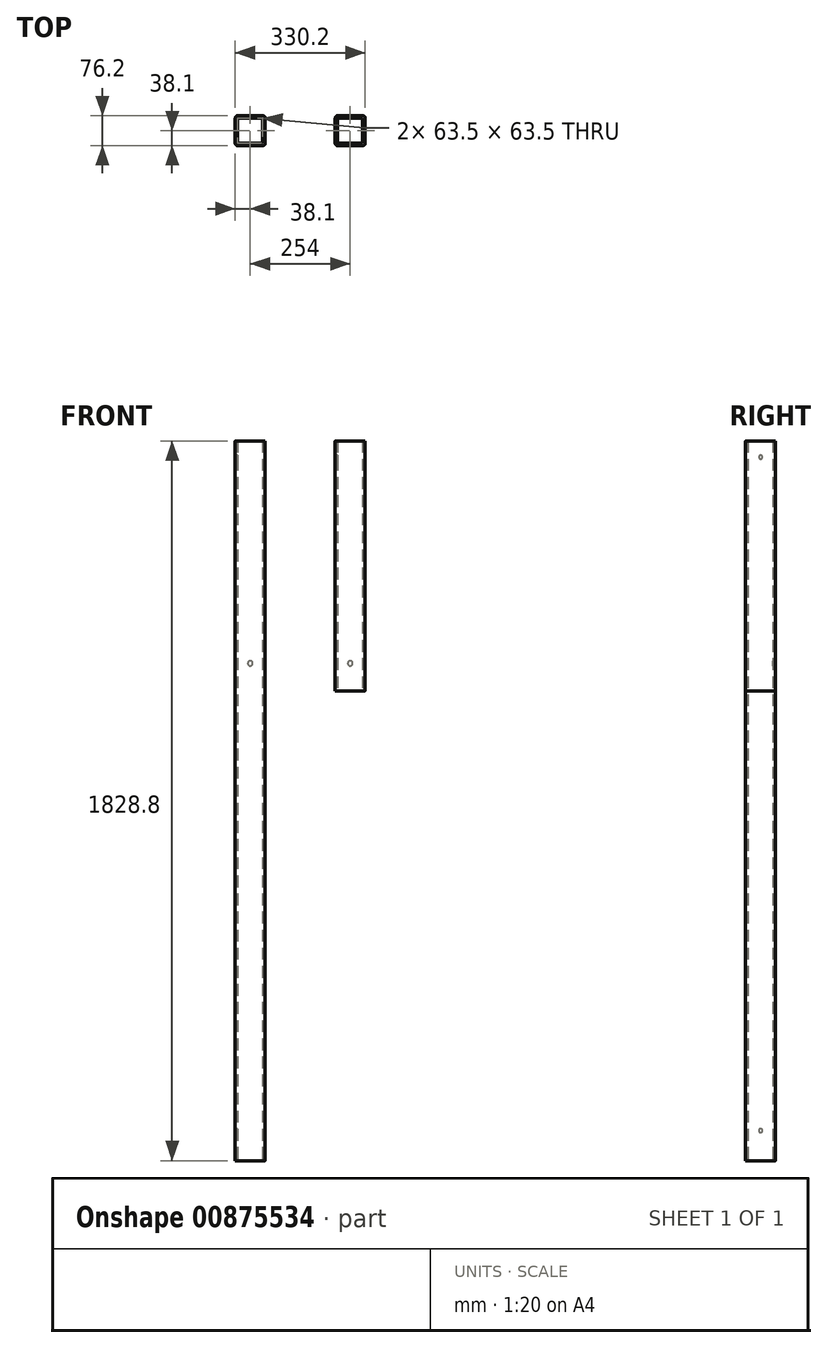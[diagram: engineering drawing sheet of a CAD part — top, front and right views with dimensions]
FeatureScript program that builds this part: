
annotation { "Feature Type Name" : "Feature", "Feature Type Description" : "" }
export const myFeature = defineFeature(function(context is Context, id is Id, definition is map)
    precondition{}
    {
        {
            var Q0;
            Q0=qCreatedBy(makeId("Top.planeOp"),FACE);
            var sketch = newSketch(context, id + "F0", { "sketchPlane" : qUnion([Q0])});
            skLineSegment(sketch, "E0.bottom", {"start": v(31.75, -38.1) * mm, "end": v(-31.75, -38.1) * mm});
            skLineSegment(sketch, "E0.top", {"start": v(31.75, 38.1) * mm, "end": v(-31.75, 38.1) * mm});
            skLineSegment(sketch, "E0.left", {"start": v(38.1, -31.75) * mm, "end": v(38.1, 31.75) * mm});
            skLineSegment(sketch, "E0.right", {"start": v(-38.1, -31.75) * mm, "end": v(-38.1, 31.75) * mm});
            skPoint(sketch, "E0.middle", {"position": v(0, 0) * mm});
            skLineSegment(sketch, "E1.bottom", {"start": v(31.75, -31.75) * mm, "end": v(-31.75, -31.75) * mm});
            skLineSegment(sketch, "E1.top", {"start": v(31.75, 31.75) * mm, "end": v(-31.75, 31.75) * mm});
            skLineSegment(sketch, "E1.left", {"start": v(31.75, -31.75) * mm, "end": v(31.75, 31.75) * mm});
            skLineSegment(sketch, "E1.right", {"start": v(-31.75, -31.75) * mm, "end": v(-31.75, 31.75) * mm});
            skPoint(sketch, "E2.visualSharp", {"position": v(-38.1, 38.1) * mm});
            skArc(sketch, "E2.filletArc", {"start": v(-31.75, 38.1) * mm, "mid": v(-36.24, 36.24) * mm, "end": v(-38.1, 31.75) * mm});
            skPoint(sketch, "E3.visualSharp", {"position": v(38.1, 38.1) * mm});
            skArc(sketch, "E3.filletArc", {"start": v(38.1, 31.75) * mm, "mid": v(36.24, 36.24) * mm, "end": v(31.75, 38.1) * mm});
            skPoint(sketch, "E4.visualSharp", {"position": v(38.1, -38.1) * mm});
            skArc(sketch, "E4.filletArc", {"start": v(31.75, -38.1) * mm, "mid": v(36.24, -36.24) * mm, "end": v(38.1, -31.75) * mm});
            skPoint(sketch, "E5.visualSharp", {"position": v(-38.1, -38.1) * mm});
            skArc(sketch, "E5.filletArc", {"start": v(-38.1, -31.75) * mm, "mid": v(-36.24, -36.24) * mm, "end": v(-31.75, -38.1) * mm});
            skSolve(sketch);
        }
        {
            var Q0;
            Q0=makeQuery(id+"F0.imprint","IMPRINT",FACE,{"disambiguationData":[TD([[makeQuery(id+"F0.imprint","IMPRINT",EDGE,{"derivedFrom":sQuery(id+"F0.wireOp",EDGE,"E0.bottom")}),-1.0]])]});
            extrude(context, id + "F1", {"entities" : qUnion([Q0]), "endBound" : BoundingType.SYMMETRIC, "depth" : 1828.8 * mm, "offsetDistance" : 25.4 * mm});
        }
        {
            var Q0;
            Q0=makeQuery(id+"F1.opExtrude","SWEPT_FACE",FACE,{"disambiguationData":[OSD([sQuery(id+"F0.wireOp",EDGE,"E0.top")])]});
            var sketch = newSketch(context, id + "F2", { "sketchPlane" : qUnion([Q0])});
            skCircle(sketch, "E6", {"center": v(0, 349.25) * mm, "radius": 6.35 * mm});
            skLineSegment(sketch, "E7", {"start": v(0, 914.4) * mm, "end": v(0, 349.25) * mm});
            skSolve(sketch);
        }
        {
            var Q0;
            Q0=makeQuery(id+"F2.imprint","IMPRINT",FACE,{"disambiguationData":[TD([[makeQuery(id+"F2.imprint","IMPRINT",EDGE,{"derivedFrom":sQuery(id+"F2.wireOp",EDGE,"E6")}),1.0]])]});
            var Q1;
            Q1=makeQuery(id+"F1.opExtrude","SWEPT_FACE",FACE,{"disambiguationData":[OSD([sQuery(id+"F0.wireOp",EDGE,"E1.top")])]});
            extrude(context, id + "F3", {"entities" : qUnion([Q0]), "operationType" : NewBodyOperationType.REMOVE, "endBound" : BoundingType.UP_TO_SURFACE, "oppositeDirection" : true, "depth" : 25.4 * mm, "endBoundEntityFace" : qUnion([Q1]), "offsetDistance" : 25.4 * mm});
        }
        {
            var Q0;
            Q0=makeQuery(id+"F1.opExtrude","SWEPT_FACE",FACE,{"disambiguationData":[OSD([sQuery(id+"F0.wireOp",EDGE,"E0.right")])]});
            var sketch = newSketch(context, id + "F4", { "sketchPlane" : qUnion([Q0])});
            skCircle(sketch, "E8", {"center": v(0, -838.2) * mm, "radius": 4.76 * mm});
            skLineSegment(sketch, "E9", {"start": v(0, -838.2) * mm, "end": v(0, -914.4) * mm});
            skSolve(sketch);
        }
        {
            var Q0;
            Q0=makeQuery(id+"F4.imprint","IMPRINT",FACE,{"disambiguationData":[TD([[makeQuery(id+"F4.imprint","IMPRINT",EDGE,{"derivedFrom":sQuery(id+"F4.wireOp",EDGE,"E8")}),1.0]])]});
            var Q1;
            Q1=makeQuery(id+"F1.opExtrude","SWEPT_FACE",FACE,{"disambiguationData":[OSD([sQuery(id+"F0.wireOp",EDGE,"E1.right")])]});
            extrude(context, id + "F5", {"entities" : qUnion([Q0]), "operationType" : NewBodyOperationType.REMOVE, "endBound" : BoundingType.UP_TO_SURFACE, "oppositeDirection" : true, "depth" : 25.4 * mm, "endBoundEntityFace" : qUnion([Q1]), "offsetDistance" : 25.4 * mm});
        }
        {
            var Q0;
            Q0=makeQuery(id+"F1.opExtrude","SWEPT_FACE",FACE,{"disambiguationData":[OSD([sQuery(id+"F0.wireOp",EDGE,"E0.right")])]});
            var sketch = newSketch(context, id + "F6", { "sketchPlane" : qUnion([Q0])});
            skLineSegment(sketch, "E10", {"start": v(0, 914.4) * mm, "end": v(0, 873.13) * mm});
            skCircle(sketch, "E11", {"center": v(0, 873.13) * mm, "radius": 4.76 * mm});
            skSolve(sketch);
        }
        {
            var Q0;
            Q0=makeQuery(id+"F6.imprint","IMPRINT",FACE,{"disambiguationData":[TD([[makeQuery(id+"F6.imprint","IMPRINT",EDGE,{"derivedFrom":sQuery(id+"F6.wireOp",EDGE,"E11")}),1.0]])]});
            extrude(context, id + "F7", {"entities" : qUnion([Q0]), "operationType" : NewBodyOperationType.REMOVE, "endBound" : BoundingType.UP_TO_NEXT, "oppositeDirection" : true, "depth" : 25.4 * mm, "offsetDistance" : 25.4 * mm});
        }
        {
            var Q0;
            Q0=makeQuery(id+"F1.opExtrude","SWEPT_BODY",BODY,{"disambiguationData":[OSD([sQuery(id+"F0.wireOp",EDGE,"E0.bottom"),sQuery(id+"F0.wireOp",EDGE,"E0.top"),sQuery(id+"F0.wireOp",EDGE,"E0.left"),sQuery(id+"F0.wireOp",EDGE,"E0.right"),sQuery(id+"F0.wireOp",EDGE,"E1.bottom"),sQuery(id+"F0.wireOp",EDGE,"E1.top"),sQuery(id+"F0.wireOp",EDGE,"E1.left"),sQuery(id+"F0.wireOp",EDGE,"E1.right"),sQuery(id+"F0.wireOp",EDGE,"E2.filletArc"),sQuery(id+"F0.wireOp",EDGE,"E3.filletArc"),sQuery(id+"F0.wireOp",EDGE,"E4.filletArc"),sQuery(id+"F0.wireOp",EDGE,"E5.filletArc")])]});
            transform(context, id + "F8", {"entities" : qUnion([Q0]), "transformType" : TransformType.TRANSLATION_3D, "dx" : 254 * mm, "dy" : 0 * mm, "dz" : 0 * mm, "makeCopy" : true});
        }
        {
            var Q0;
            Q0=makeQuery(id+"F8.opPattern","COPY",FACE,{"derivedFrom":makeQuery(id+"F1.opExtrude","CAP_FACE",FACE,{"disambiguationData":[OSD([sQuery(id+"F0.wireOp",EDGE,"E0.bottom"),sQuery(id+"F0.wireOp",EDGE,"E0.top"),sQuery(id+"F0.wireOp",EDGE,"E0.left"),sQuery(id+"F0.wireOp",EDGE,"E0.right"),sQuery(id+"F0.wireOp",EDGE,"E1.bottom"),sQuery(id+"F0.wireOp",EDGE,"E1.top"),sQuery(id+"F0.wireOp",EDGE,"E1.left"),sQuery(id+"F0.wireOp",EDGE,"E1.right"),sQuery(id+"F0.wireOp",EDGE,"E2.filletArc"),sQuery(id+"F0.wireOp",EDGE,"E3.filletArc"),sQuery(id+"F0.wireOp",EDGE,"E4.filletArc"),sQuery(id+"F0.wireOp",EDGE,"E5.filletArc")])],"isStart":true}),"instanceName":"1"});
            extrude(context, id + "F9", {"entities" : qUnion([Q0]), "operationType" : NewBodyOperationType.REMOVE, "oppositeDirection" : true, "depth" : 1193.8 * mm, "offsetDistance" : 25.4 * mm});
        }
    });
